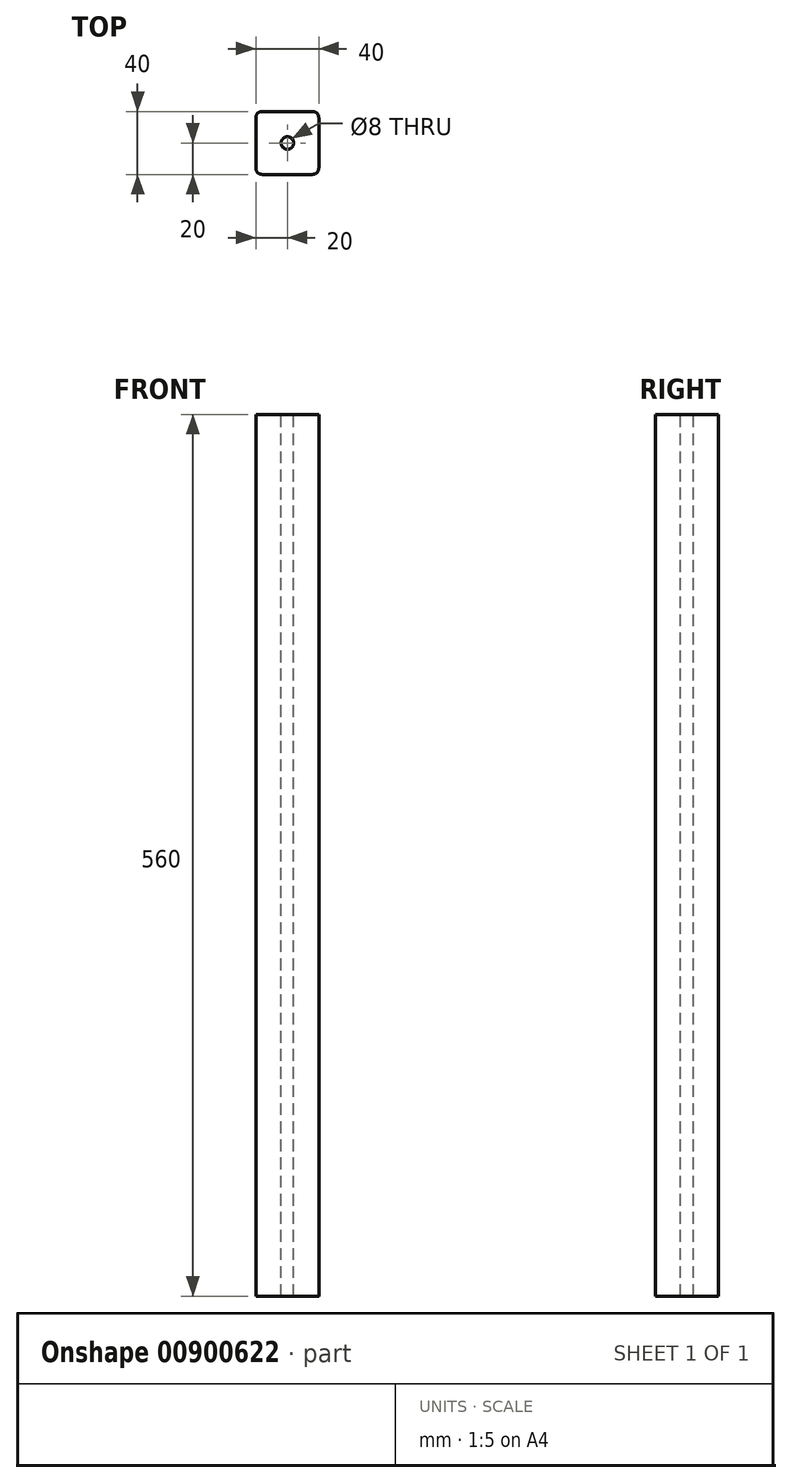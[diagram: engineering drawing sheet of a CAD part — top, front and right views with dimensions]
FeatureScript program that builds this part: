
annotation { "Feature Type Name" : "Feature", "Feature Type Description" : "" }
export const myFeature = defineFeature(function(context is Context, id is Id, definition is map)
    precondition{}
    {
        {
            var Q0;
            Q0=qCreatedBy(makeId("Top.planeOp"),FACE);
            var sketch = newSketch(context, id + "F0", { "sketchPlane" : qUnion([Q0])});
            skLineSegment(sketch, "E0.bottom", {"start": v(20, -20) * mm, "end": v(-20, -20) * mm});
            skLineSegment(sketch, "E0.top", {"start": v(20, 20) * mm, "end": v(-20, 20) * mm});
            skLineSegment(sketch, "E0.left", {"start": v(20, -20) * mm, "end": v(20, 20) * mm});
            skLineSegment(sketch, "E0.right", {"start": v(-20, -20) * mm, "end": v(-20, 20) * mm});
            skPoint(sketch, "E0.middle", {"position": v(0, 0) * mm});
            skSolve(sketch);
        }
        {
            var Q0;
            Q0=makeQuery(id+"F0.imprint","IMPRINT",FACE,{"disambiguationData":[TD([[makeQuery(id+"F0.imprint","IMPRINT",EDGE,{"derivedFrom":sQuery(id+"F0.wireOp",EDGE,"E0.bottom")}),-1.0]])]});
            extrude(context, id + "F1", {"entities" : qUnion([Q0]), "depth" : 560 * mm, "offsetDistance" : 25 * mm});
        }
        {
            var Q0;
            Q0=makeQuery(id+"F1.opExtrude","CAP_FACE",FACE,{"disambiguationData":[OSD([sQuery(id+"F0.wireOp",EDGE,"E0.bottom"),sQuery(id+"F0.wireOp",EDGE,"E0.top"),sQuery(id+"F0.wireOp",EDGE,"E0.left"),sQuery(id+"F0.wireOp",EDGE,"E0.right")])],"isStart":false});
            var sketch = newSketch(context, id + "F2", { "sketchPlane" : qUnion([Q0])});
            skPoint(sketch, "E1", {"position": v(0, 0) * mm});
            skSolve(sketch);
        }
        {
            var Q0;
            Q0=sQuery(id+"F2.wireOp",VERTEX,"E1");
            var Q1;
            Q1=makeQuery(id+"F1.opExtrude","SWEPT_BODY",BODY,{"disambiguationData":[OSD([sQuery(id+"F0.wireOp",EDGE,"E0.bottom"),sQuery(id+"F0.wireOp",EDGE,"E0.top"),sQuery(id+"F0.wireOp",EDGE,"E0.left"),sQuery(id+"F0.wireOp",EDGE,"E0.right")])]});
            hole(context, id + "F3", {"style" : HoleStyle.SIMPLE, "endStyle" : HoleEndStyle.THROUGH, "holeDiameter" : 8 * mm, "majorDiameter" : 5 * mm, "isTappedThrough" : true, "tappedDepth" : 12 * mm, "tapClearance" : 3, "locations" : qUnion([Q0]), "scope" : qUnion([Q1])});
        }
        {
            var Q0;
            Q0=makeQuery(id+"F1.opExtrude","SWEPT_EDGE",EDGE,{"disambiguationData":[OSD([sQuery(id+"F0.wireOp",EDGE,"E0.bottom"),sQuery(id+"F0.wireOp",EDGE,"E0.left")])]});
            var Q1;
            Q1=makeQuery(id+"F1.opExtrude","SWEPT_EDGE",EDGE,{"disambiguationData":[OSD([sQuery(id+"F0.wireOp",EDGE,"E0.bottom"),sQuery(id+"F0.wireOp",EDGE,"E0.right")])]});
            var Q2;
            Q2=makeQuery(id+"F1.opExtrude","SWEPT_EDGE",EDGE,{"disambiguationData":[OSD([sQuery(id+"F0.wireOp",EDGE,"E0.top"),sQuery(id+"F0.wireOp",EDGE,"E0.left")])]});
            var Q3;
            Q3=makeQuery(id+"F1.opExtrude","SWEPT_EDGE",EDGE,{"disambiguationData":[OSD([sQuery(id+"F0.wireOp",EDGE,"E0.top"),sQuery(id+"F0.wireOp",EDGE,"E0.right")])]});
            fillet(context, id + "F4", {"entities" : qUnion([Q0, Q1, Q2, Q3]), "radius" : 4 * mm, "tangentPropagation" : true, "allowEdgeOverflow" : false});
        }
    });
